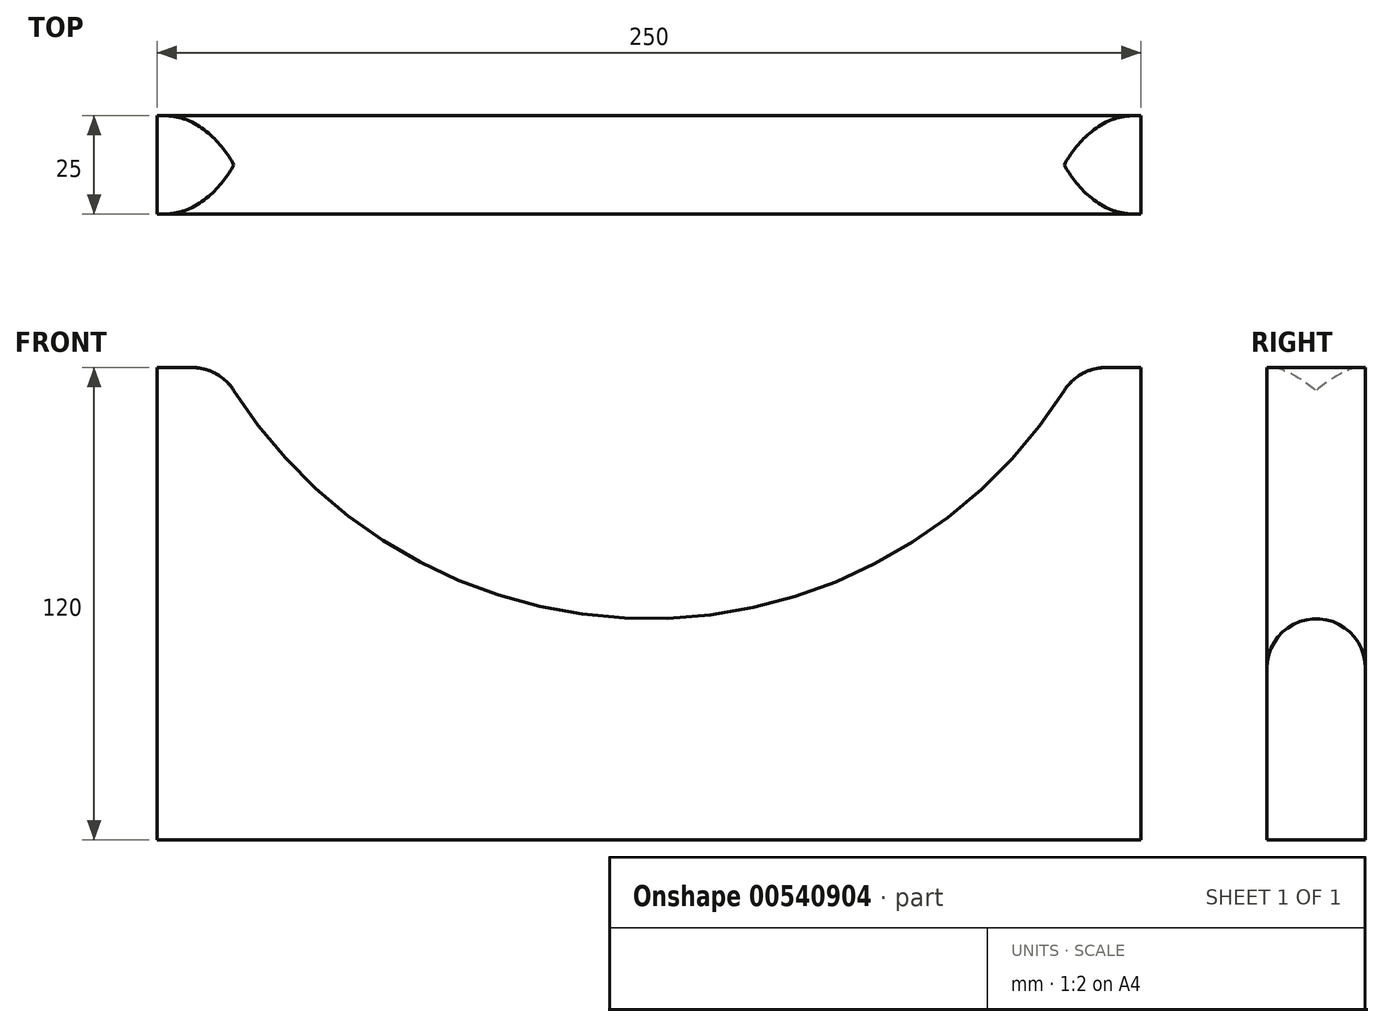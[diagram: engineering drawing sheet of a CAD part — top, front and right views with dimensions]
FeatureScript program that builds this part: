
annotation { "Feature Type Name" : "Feature", "Feature Type Description" : "" }
export const myFeature = defineFeature(function(context is Context, id is Id, definition is map)
    precondition{}
    {
        {
            var Q0;
            Q0=qCreatedBy(makeId("Front.planeOp"),FACE);
            var sketch = newSketch(context, id + "F0", { "sketchPlane" : qUnion([Q0])});
            skLineSegment(sketch, "E0.bottom", {"start": v(-277.96, -123.72) * mm, "end": v(-27.96, -123.72) * mm});
            skLineSegment(sketch, "E0.left", {"start": v(-277.96, -123.72) * mm, "end": v(-277.96, -3.72) * mm});
            skLineSegment(sketch, "E0.right", {"start": v(-27.96, -123.72) * mm, "end": v(-27.96, -3.72) * mm});
            skLineSegment(sketch, "E1", {"start": v(-27.96, -3.72) * mm, "end": v(-43.96, -3.72) * mm});
            skLineSegment(sketch, "E2", {"start": v(-277.96, -3.72) * mm, "end": v(-261.96, -3.72) * mm});
            skArc(sketch, "E3.trimOffspring", {"start": v(-261.96, -3.72) * mm, "mid": v(-152.96, -67.53) * mm, "end": v(-43.96, -3.72) * mm});
            skLineSegment(sketch, "E4.trimOffspring", {"start": v(-261.96, -3.72) * mm, "end": v(-277.96, -3.72) * mm});
            skSolve(sketch);
        }
        {
            var Q0;
            Q0 = qSketchRegion(id + "F0", true);
            extrude(context, id + "F1", {"entities" : qUnion([Q0]), "depth" : 25 * mm, "offsetDistance" : 25 * mm});
        }
        {
            var Q0;
            Q0=makeQuery(id+"F1.opExtrude","SWEPT_EDGE",EDGE,{"disambiguationData":[OSD([sQuery(id+"F0.wireOp",EDGE,"E3.trimOffspring"),sQuery(id+"F0.wireOp",EDGE,"E4.trimOffspring")])]});
            var Q1;
            Q1=makeQuery(id+"F1.opExtrude","SWEPT_EDGE",EDGE,{"disambiguationData":[OSD([sQuery(id+"F0.wireOp",EDGE,"E1"),sQuery(id+"F0.wireOp",EDGE,"E3.trimOffspring")])]});
            var Q2;
            Q2=makeQuery(id+"F1.opExtrude","CAP_EDGE",EDGE,{"disambiguationData":[OSD([sQuery(id+"F0.wireOp",EDGE,"E3.trimOffspring")])],"isStart":false});
            var Q3;
            Q3=makeQuery(id+"F1.opExtrude","CAP_EDGE",EDGE,{"disambiguationData":[OSD([sQuery(id+"F0.wireOp",EDGE,"E3.trimOffspring")])],"isStart":true});
            fillet(context, id + "F2", {"entities" : qUnion([Q0, Q1, Q2, Q3]), "radius" : 12.5 * mm, "tangentPropagation" : true, "allowEdgeOverflow" : false});
        }
    });
